# Revit family: HVAC_Fan-Assisted-Distributors_Neptronic_SKH4_ADU-1000
name_source: partatom
category: Mechanical Equipment
units: mm (PartAtom-declared; Revit-internal decimal feet)

## family parameters
Classification = None
Cut with Voids When Loaded = No
Host = Face
OmniClass Number = 23.33.27.15
Part Type = Normal
Room Calculation Point = No
Round Connector Dimension = Use Diameter
Shared = No

## types (2) — shared parameters
CFM = 1000 CFM
Default Elevation = 48.00 in
Depth = 0.00 in
Description = Axial projection mist distributor
Diameter = 18.30 in
Frequency = 50 Hz
Height = 8.40 in
Length = 0.00 in
Manufacturer = Neptronic
Model Type = ADU
Mounting Type = Wall Mounted
Nozzle Capacity = 33lb/h to 50lb/h
Number of Poles = 1
Number of Spray Nozzles = 5
Plumbing Connection Diameter = 0.70 in
Power Factor = 1
Product Material = Neptronic - Stainless steel
Product Page URL = https://www.neptronic.com
RLA = 1 A
URL = https://www.neptronic.com
Version = 1
Weight = 17.00 lb
Width = 0.00 in

## per-type parameters (varying)
| type | Apparent Load | Supply Voltage | Voltage |
| SKH4-ADU-1000-A-5 | 168 VA | A | 120 V |
| SKH4-ADU-1000-C-5 | 120 VA | C | 240 V |

note: column(s) folded — value = type name in every type: Model

## geometry (parser evidence)
native form markers: Sweep x4
no freeform markers — native parametric forms only
